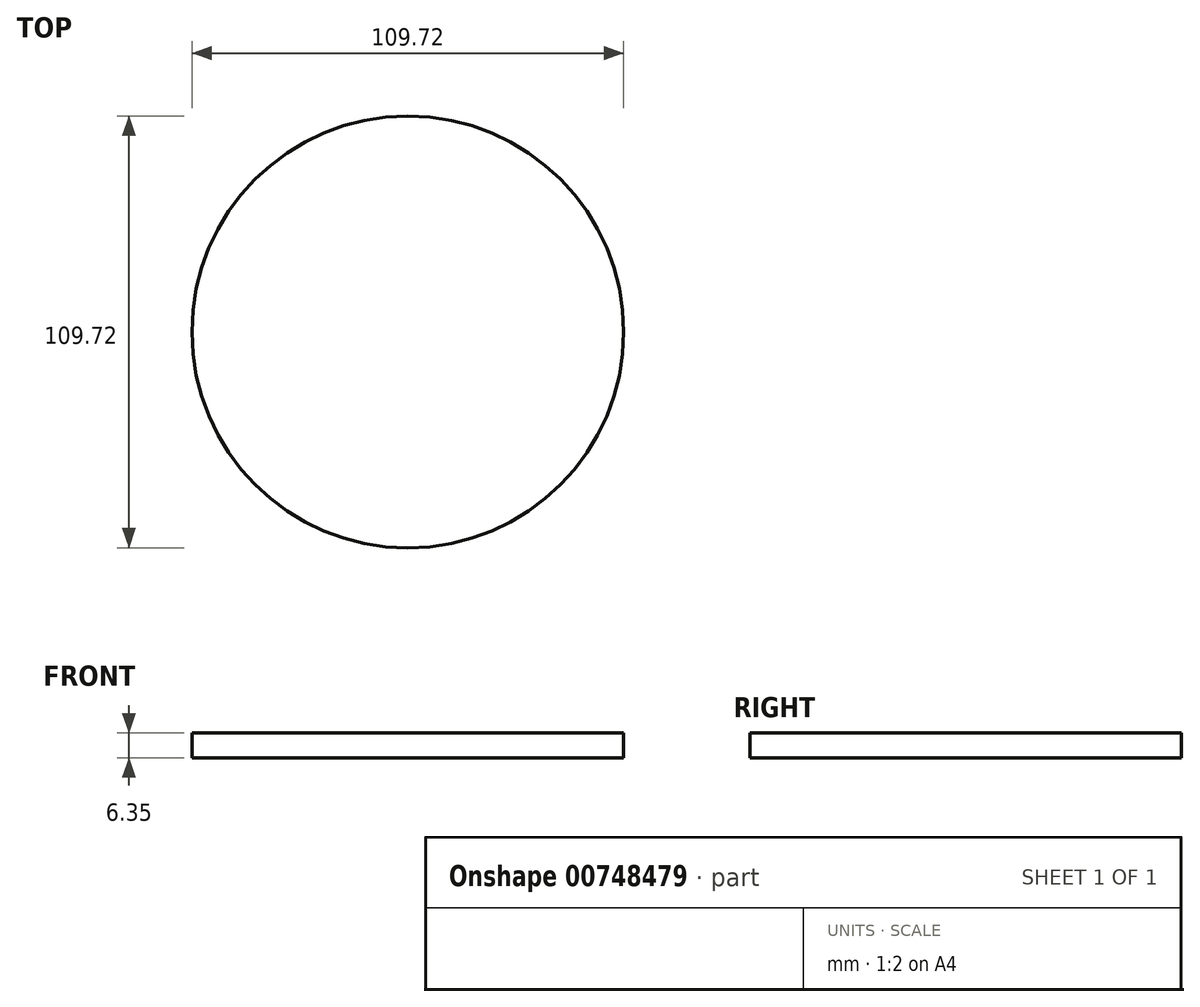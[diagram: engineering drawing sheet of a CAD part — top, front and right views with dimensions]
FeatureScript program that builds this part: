
annotation { "Feature Type Name" : "Feature", "Feature Type Description" : "" }
export const myFeature = defineFeature(function(context is Context, id is Id, definition is map)
    precondition{}
    {
        {
            var Q0;
            Q0=qCreatedBy(makeId("Top.planeOp"),FACE);
            var sketch = newSketch(context, id + "F0", { "sketchPlane" : qUnion([Q0])});
            skCircle(sketch, "E0", {"center": v(0, 0) * mm, "radius": 54.86 * mm});
            skSolve(sketch);
        }
        {
            var Q0;
            Q0=makeQuery(id+"F0.imprint","IMPRINT",FACE,{"disambiguationData":[TD([[makeQuery(id+"F0.imprint","IMPRINT",EDGE,{"derivedFrom":sQuery(id+"F0.wireOp",EDGE,"E0")}),1.0]])]});
            var sketch = newSketch(context, id + "F1", { "sketchPlane" : qUnion([Q0])});
            skSolve(sketch);
        }
        {
            var Q0;
            Q0=makeQuery(id+"F1.imprint","IMPRINT",FACE,{"disambiguationData":[TD([[makeQuery(id+"F1.imprint","IMPRINT",EDGE,{"derivedFrom":makeQuery(id+"F0.imprint","IMPRINT",EDGE,{"derivedFrom":sQuery(id+"F0.wireOp",EDGE,"E0")})}),1.0]])]});
            extrude(context, id + "F2", {"entities" : qUnion([Q0]), "depth" : 6.35 * mm, "offsetDistance" : 25.4 * mm});
        }
    });
